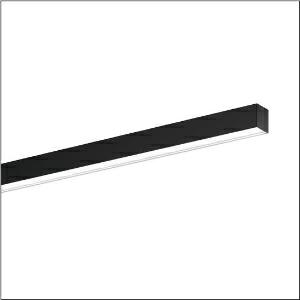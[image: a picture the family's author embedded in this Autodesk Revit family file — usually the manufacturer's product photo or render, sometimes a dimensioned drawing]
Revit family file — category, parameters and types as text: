
# Revit family: silica_21_51mx20dc45bb
name_source: partatom
category: Lighting Fixtures
units: mm (PartAtom-declared; Revit-internal decimal feet)

## family parameters
Cut with Voids When Loaded = No
Host = Face
Light Source = No
Part Type = Normal
Room Calculation Point = No
Round Connector Dimension = Use Diameter
Shared = No

## types (1)
- --- (1 x LED, 6000 lm, 40.1 W, 4000K)
    Apparent Load = 40 VA
    CIE Flux Codes = 48 79 96 100 100
    Color Rendering = 80
    Color Temperature = 4000K
    Default Elevation = 1800 mm
    Description = Silica 21, office luminaire, primary optical cover: cover, of PMMA, opal, light emission: direct distribution, primary light characteristic: symmetric, installation type: surface-mounted, LED, rated luminous flux: 6.000lm, luminous efficacy: 150lm/W, light colour: 840, colour temperature: 4000K, control gear: DALI 2, with terminal, 3+2-pole, max. 2.5mm², mains connection: 220..240V, AC, 50/60Hz, rated input power: 40.1W, luminaire housing, of aluminium, matt jet black (RAL 9005), length: 3.004mm, width: 53mm, height: 53mm, protection rating (complete): IP20, insulation class (complete): insulation class I (protective earthing), certification: CE, permissible operating ambient temperature: 0..+35°C, standard: EN 50419, packaging unit: 1 piece
    Height = 53 mm
    Lamp = 1 x LED
    Lamp Light Flux = 6000 lm
    Lamp Power = 40.1 W
    Lamp count = 1
    Length = 3004 mm
    Luminous efficacy = 150 lm/W
    Manufacturer = Siteco
    ModVariant = No
    Model = 51MX20DC45BB
    Mounting Place = Ceiling
    Mounting Type = Surface mounted
    Number of Poles = 1
    OnlyDefault = Yes
    Power Factor = 1
    Product Name = Silica 21
    Product group = office luminaire | ceiling mounted
    ProductGroupID = 301
    Protection Class = Protection class I
    Protection Degree = IP 20
    RLX_Detail_Level = 1
    RLX_Emergency_Light_Flux = 0 lm
    RLX_Emergency_Type = 0
    RLX_Emergency_Type_DB = No
    RlxData = <blob elided: 28789 chars, md5=39c20ddc>
    Socket = socket
    Standby Power = 0 W
    System Light Flux = 6000 lm
    System Power = 40 W
    Type Comments = factory setting: luminous flux: 100 % | dim-lin: 254 | 218 mA
    Type Image = l_1335925.jpg
    URL = http://relux.com
    VarID = @adj_119567
    Voltage = 0 V
    Weight = 0.00 kg
    Width = 53 mm

## geometry (parser evidence)
native form markers: Blend x4, Sweep x9
no freeform markers — native parametric forms only
